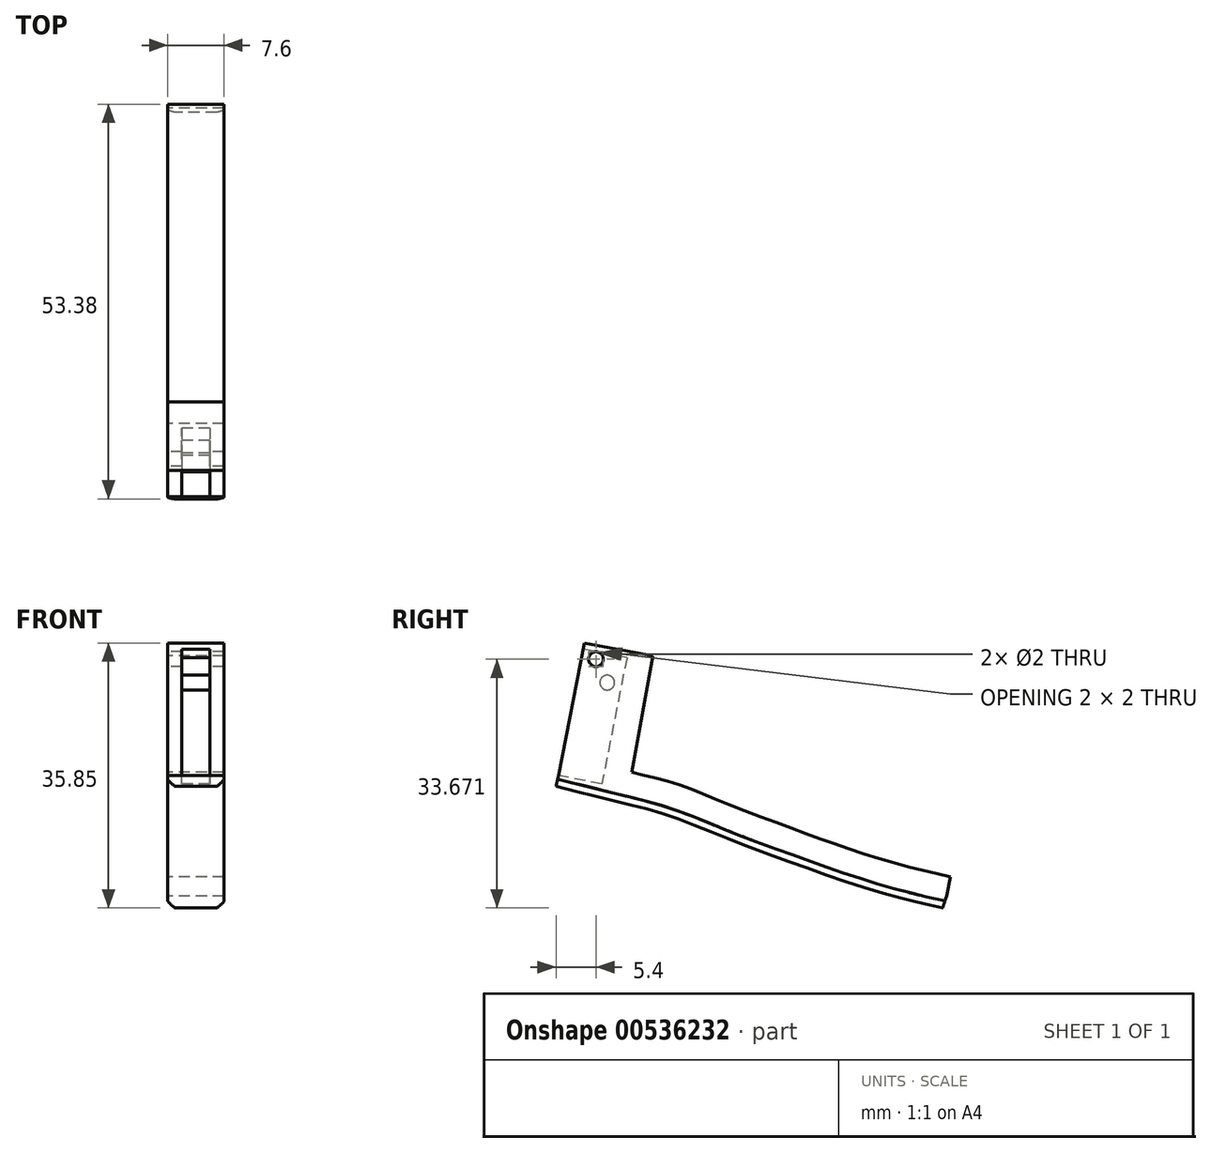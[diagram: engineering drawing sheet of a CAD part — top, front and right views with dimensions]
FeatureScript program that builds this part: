
annotation { "Feature Type Name" : "Feature", "Feature Type Description" : "" }
export const myFeature = defineFeature(function(context is Context, id is Id, definition is map)
    precondition{}
    {
        {
            var Q0;
            Q0=qCreatedBy(makeId("Right.planeOp"),FACE);
            var sketch = newSketch(context, id + "F0", { "sketchPlane" : qUnion([Q0])});
            skLineSegment(sketch, "E0", {"start": v(39.57, -26.04) * mm, "end": v(40.1, -23.42) * mm});
            skFitSpline(sketch, "E1", {"points": [v(40.1, -23.42) * mm, v(33, -21.7) * mm, v(24.77, -19.1) * mm, v(17.18, -16.34) * mm, v(8.35, -12.93) * mm, v(3.23, -10.92) * mm, v(-2.2, -9.48) * mm, v(-5.65, -8.47) * mm], "startDerivative": vector(-46.66, 10.42) * mm, "endDerivative": vector(-30.73, 9.5) * mm});
            skLineSegment(sketch, "E2", {"start": v(-5.65, -8.47) * mm, "end": v(-2.8, 6.98) * mm});
            skLineSegment(sketch, "E3", {"start": v(-2.8, 6.98) * mm, "end": v(-9.43, 8.2) * mm});
            skLineSegment(sketch, "E4", {"start": v(-9.43, 8.2) * mm, "end": v(-12.96, -9.7) * mm});
            skLineSegment(sketch, "E5", {"start": v(-12.96, -9.7) * mm, "end": v(-13.28, -11.2) * mm});
            skFitSpline(sketch, "E6", {"points": [v(-13.28, -11.2) * mm, v(-3.91, -13.5) * mm, v(2.64, -15.36) * mm, v(10.1, -18.33) * mm, v(16.31, -20.65) * mm, v(25.26, -23.84) * mm, v(34.06, -26.49) * mm, v(39.02, -27.64) * mm], "startDerivative": vector(61.98, -15.2) * mm, "endDerivative": vector(39.85, -8.64) * mm});
            skLineSegment(sketch, "E7", {"start": v(39.02, -27.64) * mm, "end": v(39.57, -26.04) * mm});
            skSolve(sketch);
        }
        {
            var Q0;
            Q0 = qSketchRegion(id + "F0", true);
            extrude(context, id + "F1", {"entities" : qUnion([Q0]), "depth" : 7.6 * mm, "offsetDistance" : 25 * mm});
        }
        {
            var Q0;
            Q0=makeQuery(id+"F1.opExtrude","SWEPT_FACE",FACE,{"disambiguationData":[OSD([sQuery(id+"F0.wireOp",EDGE,"E4")])]});
            var sketch = newSketch(context, id + "F2", { "sketchPlane" : qUnion([Q0])});
            skLineSegment(sketch, "E8", {"start": v(3.8, 6.22) * mm, "end": v(1.9, 6.22) * mm});
            skLineSegment(sketch, "E9", {"start": v(1.9, 6.22) * mm, "end": v(5.7, 6.22) * mm});
            skLineSegment(sketch, "E10", {"start": v(5.7, 6.22) * mm, "end": v(5.7, -12.03) * mm});
            skLineSegment(sketch, "E11", {"start": v(5.7, -12.03) * mm, "end": v(1.9, -12.03) * mm});
            skLineSegment(sketch, "E12", {"start": v(1.9, -12.03) * mm, "end": v(1.9, 6.22) * mm});
            skLineSegment(sketch, "E13", {"start": v(5.7, 5.4) * mm, "end": v(1.9, 5.4) * mm});
            skSolve(sketch);
        }
        {
            var Q0;
            Q0=makeQuery(id+"F1.opExtrude","SWEPT_FACE",FACE,{"disambiguationData":[OSD([sQuery(id+"F0.wireOp",EDGE,"E2")])]});
            extrude(context, id + "F3", {"entities" : qUnion([Q0]), "operationType" : NewBodyOperationType.ADD, "depth" : 2.7 * mm, "offsetDistance" : 25 * mm});
        }
        {
            var Q0;
            Q0=makeQuery(id+"F3.opExtrude","SWEPT_FACE",FACE,{"disambiguationData":[OSD([sQuery(id+"F0.wireOp",EDGE,"E1"),sQuery(id+"F0.wireOp",EDGE,"E2")])]});
            extrude(context, id + "F4", {"entities" : qUnion([Q0]), "operationType" : NewBodyOperationType.ADD, "depth" : 1.1 * mm, "offsetDistance" : 25 * mm});
        }
        {
            var Q0;
            {var subQ0=sQuery(id+"F2.wireOp",EDGE,"E11");Q0=makeQuery(id+"F2.imprint","IMPRINT",FACE,{"disambiguationData":[TD([[makeQuery(id+"F2.imprint","IMPRINT",EDGE,{"derivedFrom":subQ0}),-1.0]])]});}
            extrude(context, id + "F5", {"entities" : qUnion([Q0]), "operationType" : NewBodyOperationType.REMOVE, "oppositeDirection" : true, "depth" : 6 * mm, "offsetDistance" : 25 * mm});
        }
        {
            var Q0;
            {var subQ0=sQuery(id+"F0.wireOp",EDGE,"E2");var subQ1=sQuery(id+"F0.wireOp",EDGE,"E1");Q0=makeQuery(id+"F4.boolean.opBoolean","MERGE",FACE,{"derivedFrom":[makeQuery(id+"F3.boolean.opBoolean","MERGE",FACE,{"derivedFrom":[makeQuery(id+"F1.opExtrude","CAP_FACE",FACE,{"disambiguationData":[OSD([sQuery(id+"F0.wireOp",EDGE,"E0"),subQ1,subQ0,sQuery(id+"F0.wireOp",EDGE,"E3"),sQuery(id+"F0.wireOp",EDGE,"E4"),sQuery(id+"F0.wireOp",EDGE,"E5"),sQuery(id+"F0.wireOp",EDGE,"E6"),sQuery(id+"F0.wireOp",EDGE,"E7")])],"isStart":true}),makeQuery(id+"F3.opExtrude","SWEPT_FACE",FACE,{"disambiguationData":[OSD([subQ0]),TDD([makeQuery(id+"F1.opExtrude","CAP_EDGE",EDGE,{"disambiguationData":[OSD([subQ0])],"isStart":true})])]})]}),makeQuery(id+"F4.opExtrude","SWEPT_FACE",FACE,{"disambiguationData":[OSD([subQ1,subQ0]),TDD([makeQuery(id+"F3.opExtrude","SWEPT_EDGE",EDGE,{"disambiguationData":[OSD([subQ1,subQ0]),TDD([makeQuery(id+"F1.opExtrude","CAP_VERTEX",VERTEX,{"disambiguationData":[OSD([subQ1,subQ0])],"isStart":true})])]})])]})]});}
            var sketch = newSketch(context, id + "F6", { "sketchPlane" : qUnion([Q0])});
            skCircle(sketch, "E14", {"center": v(7.88, 6.02) * mm, "radius": 1 * mm});
            skSolve(sketch);
        }
        {
            var Q0;
            Q0=makeQuery(id+"F6.imprint","IMPRINT",FACE,{"disambiguationData":[TD([[makeQuery(id+"F6.imprint","IMPRINT",EDGE,{"derivedFrom":sQuery(id+"F6.wireOp",EDGE,"E14")}),1.0]])]});
            extrude(context, id + "F7", {"entities" : qUnion([Q0]), "operationType" : NewBodyOperationType.REMOVE, "oppositeDirection" : true, "depth" : 25 * mm, "offsetDistance" : 25 * mm});
        }
        {
            var Q0;
            Q0=makeQuery(id+"F5.boolean.opBoolean","COPY",FACE,{"derivedFrom":makeQuery(id+"F5.opExtrude","SWEPT_FACE",FACE,{"disambiguationData":[OSD([sQuery(id+"F2.wireOp",EDGE,"E12")])]})});
            var sketch = newSketch(context, id + "F8", { "sketchPlane" : qUnion([Q0])});
            skCircle(sketch, "E15", {"center": v(-6.36, 2.85) * mm, "radius": 1 * mm});
            skSolve(sketch);
        }
        {
            var Q0;
            Q0=makeQuery(id+"F8.imprint","IMPRINT",FACE,{"disambiguationData":[TD([[makeQuery(id+"F8.imprint","IMPRINT",EDGE,{"derivedFrom":sQuery(id+"F8.wireOp",EDGE,"E15")}),1.0]])]});
            extrude(context, id + "F9", {"entities" : qUnion([Q0]), "operationType" : NewBodyOperationType.ADD, "depth" : 5.4 * mm, "offsetDistance" : 25 * mm});
        }
        {
            var Q0;
            Q0=makeQuery(id+"F1.opExtrude","CAP_EDGE",EDGE,{"disambiguationData":[OSD([sQuery(id+"F0.wireOp",EDGE,"E6")])],"isStart":false});
            var Q1;
            Q1=makeQuery(id+"F1.opExtrude","CAP_EDGE",EDGE,{"disambiguationData":[OSD([sQuery(id+"F0.wireOp",EDGE,"E6")])],"isStart":true});
            fillet(context, id + "F10", {"entities" : qUnion([Q0, Q1]), "radius" : 1 * mm, "tangentPropagation" : true, "rho" : .1, "crossSection" : FilletCrossSection.CONIC, "allowEdgeOverflow" : false});
        }
    });
